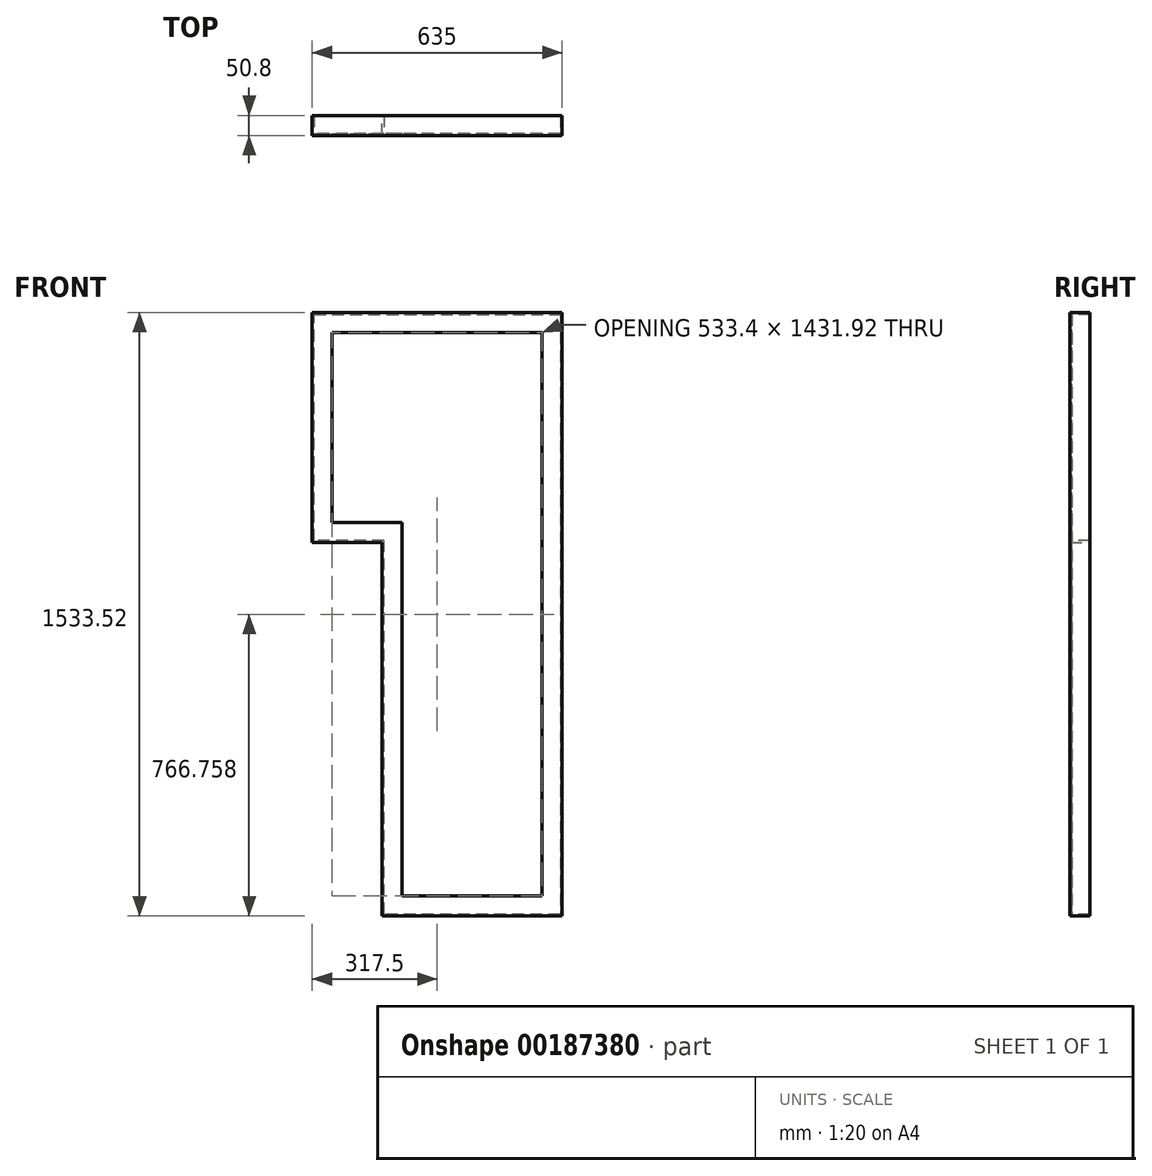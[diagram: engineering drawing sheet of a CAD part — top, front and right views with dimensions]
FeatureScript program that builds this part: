
annotation { "Feature Type Name" : "Feature", "Feature Type Description" : "" }
export const myFeature = defineFeature(function(context is Context, id is Id, definition is map)
    precondition{}
    {
        {
            var Q0;
            Q0=qCreatedBy(makeId("Front.planeOp"),FACE);
            var sketch = newSketch(context, id + "F0", { "sketchPlane" : qUnion([Q0])});
            skLineSegment(sketch, "E0", {"start": v(-177.8, 584.2) * mm, "end": v(457.2, 584.2) * mm});
            skLineSegment(sketch, "E1", {"start": v(457.2, 584.2) * mm, "end": v(457.2, -949.33) * mm});
            skLineSegment(sketch, "E2", {"start": v(457.2, -949.33) * mm, "end": v(0, -949.33) * mm});
            skLineSegment(sketch, "E3", {"start": v(0, -949.33) * mm, "end": v(0, 0) * mm});
            skLineSegment(sketch, "E4", {"start": v(0, 0) * mm, "end": v(-177.8, 0) * mm});
            skLineSegment(sketch, "E5", {"start": v(-177.8, 0) * mm, "end": v(-177.8, 584.2) * mm});
            skLineSegment(sketch, "E6.0", {"start": v(50.8, 50.8) * mm, "end": v(-127, 50.8) * mm});
            skLineSegment(sketch, "E6.1", {"start": v(-127, 533.4) * mm, "end": v(406.4, 533.4) * mm});
            skLineSegment(sketch, "E6.2", {"start": v(406.4, 533.4) * mm, "end": v(406.4, -898.53) * mm});
            skLineSegment(sketch, "E6.3", {"start": v(-127, 50.8) * mm, "end": v(-127, 533.4) * mm});
            skLineSegment(sketch, "E6.4", {"start": v(406.4, -898.53) * mm, "end": v(50.8, -898.53) * mm});
            skLineSegment(sketch, "E6.5", {"start": v(50.8, -898.53) * mm, "end": v(50.8, 50.8) * mm});
            skSolve(sketch);
        }
        {
            var Q0;
            Q0=makeQuery(id+"F0.imprint","IMPRINT",FACE,{"disambiguationData":[TD([[makeQuery(id+"F0.imprint","IMPRINT",EDGE,{"derivedFrom":sQuery(id+"F0.wireOp",EDGE,"E0")}),-1.0]])]});
            extrude(context, id + "F1", {"entities" : qUnion([Q0]), "depth" : 4.76 * mm});
        }
        {
            var Q0;
            Q0=makeQuery(id+"F1.opExtrude","CAP_FACE",FACE,{"disambiguationData":[OSD([sQuery(id+"F0.wireOp",EDGE,"E0"),sQuery(id+"F0.wireOp",EDGE,"E1"),sQuery(id+"F0.wireOp",EDGE,"E2"),sQuery(id+"F0.wireOp",EDGE,"E3"),sQuery(id+"F0.wireOp",EDGE,"E4"),sQuery(id+"F0.wireOp",EDGE,"E5"),sQuery(id+"F0.wireOp",EDGE,"E6.0"),sQuery(id+"F0.wireOp",EDGE,"E6.1"),sQuery(id+"F0.wireOp",EDGE,"E6.2"),sQuery(id+"F0.wireOp",EDGE,"E6.3"),sQuery(id+"F0.wireOp",EDGE,"E6.4"),sQuery(id+"F0.wireOp",EDGE,"E6.5")])],"isStart":true});
            var sketch = newSketch(context, id + "F2", { "sketchPlane" : qUnion([Q0])});
            skLineSegment(sketch, "E7.0", {"start": v(-457.2, 584.2) * mm, "end": v(-457.2, -949.33) * mm});
            skLineSegment(sketch, "E8.0", {"start": v(177.8, 584.2) * mm, "end": v(-457.2, 584.2) * mm});
            skLineSegment(sketch, "E9.0", {"start": v(177.8, 0) * mm, "end": v(177.8, 584.2) * mm});
            skLineSegment(sketch, "E10.0", {"start": v(0, 0) * mm, "end": v(177.8, 0) * mm});
            skLineSegment(sketch, "E11.0", {"start": v(0, -949.33) * mm, "end": v(0, 0) * mm});
            skLineSegment(sketch, "E12.0", {"start": v(-457.2, -949.33) * mm, "end": v(0, -949.33) * mm});
            skLineSegment(sketch, "E13.0", {"start": v(-452.44, -944.56) * mm, "end": v(-4.76, -944.56) * mm});
            skLineSegment(sketch, "E13.1", {"start": v(-4.76, 4.76) * mm, "end": v(173.04, 4.76) * mm});
            skLineSegment(sketch, "E13.2", {"start": v(173.04, 4.76) * mm, "end": v(173.04, 579.44) * mm});
            skLineSegment(sketch, "E13.3", {"start": v(-4.76, -944.56) * mm, "end": v(-4.76, 4.76) * mm});
            skLineSegment(sketch, "E13.4", {"start": v(173.04, 579.44) * mm, "end": v(-452.44, 579.44) * mm});
            skLineSegment(sketch, "E13.5", {"start": v(-452.44, 579.44) * mm, "end": v(-452.44, -944.56) * mm});
            skSolve(sketch);
        }
        {
            var Q0;
            Q0=makeQuery(id+"F2.imprint","IMPRINT",FACE,{"disambiguationData":[TD([[makeQuery(id+"F2.imprint","IMPRINT",EDGE,{"derivedFrom":sQuery(id+"F2.wireOp",EDGE,"E7.0")}),1.0]])]});
            extrude(context, id + "F3", {"entities" : qUnion([Q0]), "operationType" : NewBodyOperationType.ADD, "depth" : 46.04 * mm});
        }
    });
